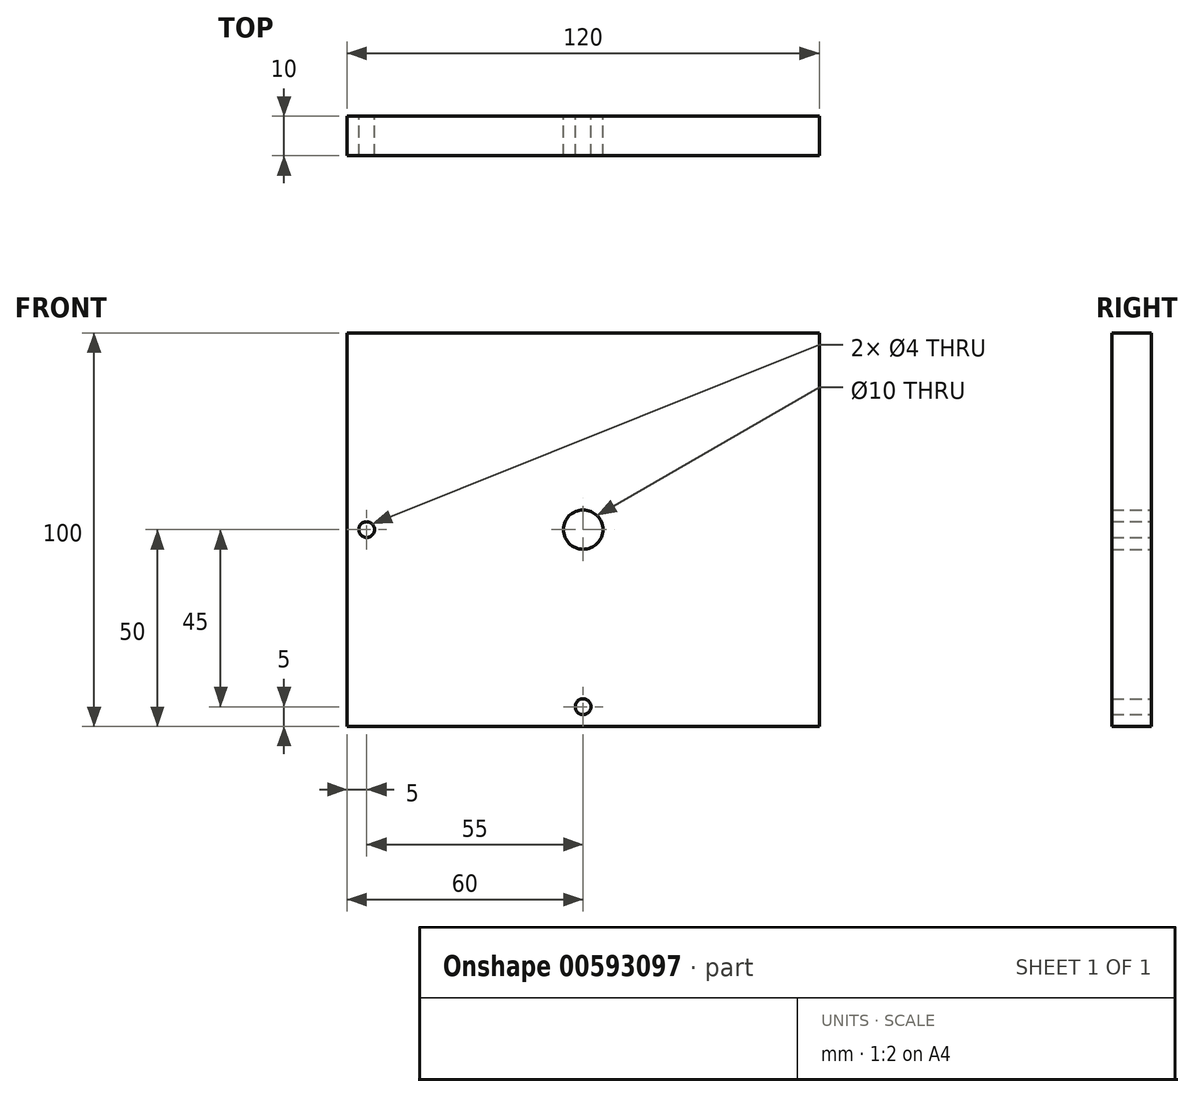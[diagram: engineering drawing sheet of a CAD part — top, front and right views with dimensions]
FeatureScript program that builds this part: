
annotation { "Feature Type Name" : "Feature", "Feature Type Description" : "" }
export const myFeature = defineFeature(function(context is Context, id is Id, definition is map)
    precondition{}
    {
        {
            var Q0;
            Q0=qCreatedBy(makeId("Front.planeOp"),FACE);
            var sketch = newSketch(context, id + "F0", { "sketchPlane" : qUnion([Q0])});
            skLineSegment(sketch, "E0.bottom", {"start": v(60, 50) * mm, "end": v(-60, 50) * mm});
            skLineSegment(sketch, "E0.top", {"start": v(60, -50) * mm, "end": v(-60, -50) * mm});
            skLineSegment(sketch, "E0.left", {"start": v(60, 50) * mm, "end": v(60, -50) * mm});
            skLineSegment(sketch, "E0.right", {"start": v(-60, 50) * mm, "end": v(-60, -50) * mm});
            skPoint(sketch, "E0.middle", {"position": v(0, 0) * mm});
            skCircle(sketch, "E1", {"center": v(-55, 0) * mm, "radius": 2 * mm});
            skCircle(sketch, "E2", {"center": v(0, 0) * mm, "radius": 5 * mm});
            skCircle(sketch, "E3", {"center": v(0, -45) * mm, "radius": 2 * mm});
            skSolve(sketch);
        }
        {
            var Q0;
            Q0=makeQuery(id+"F0.imprint","IMPRINT",FACE,{"disambiguationData":[TD([[makeQuery(id+"F0.imprint","IMPRINT",EDGE,{"derivedFrom":sQuery(id+"F0.wireOp",EDGE,"E0.bottom")}),1.0]])]});
            extrude(context, id + "F1", {"entities" : qUnion([Q0]), "depth" : 10 * mm, "offsetDistance" : 25 * mm});
        }
    });
